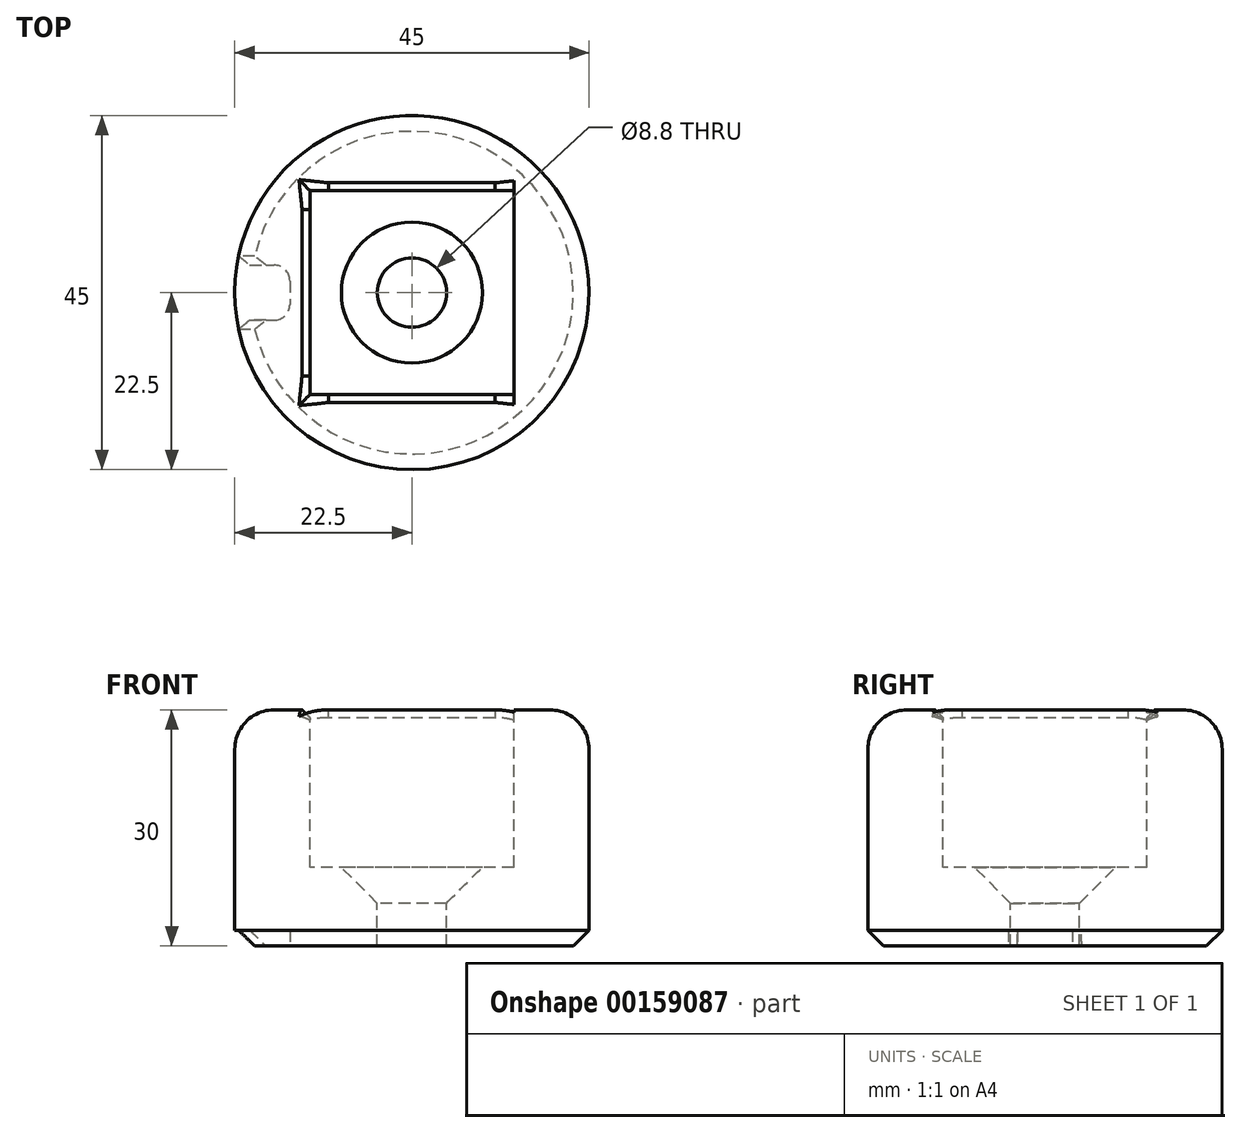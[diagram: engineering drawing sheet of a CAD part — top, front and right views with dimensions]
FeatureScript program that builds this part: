
annotation { "Feature Type Name" : "Feature", "Feature Type Description" : "" }
export const myFeature = defineFeature(function(context is Context, id is Id, definition is map)
    precondition{}
    {
        {
            var Q0;
            Q0=qCreatedBy(makeId("Top.planeOp"),FACE);
            var sketch = newSketch(context, id + "F0", { "sketchPlane" : qUnion([Q0])});
            skCircle(sketch, "E0", {"center": v(0, 0) * mm, "radius": 22.5 * mm});
            skSolve(sketch);
        }
        {
            var Q0;
            Q0=qSketchRegion(id+"F0",true);
            extrude(context, id + "F1", {"entities" : qUnion([Q0]), "depth" : 30 * mm});
        }
        {
            var Q0;
            Q0=makeQuery(id+"F1.opExtrude","CAP_FACE",FACE,{"disambiguationData":[OSD([sQuery(id+"F0.wireOp",EDGE,"E0")])],"isStart":false});
            var sketch = newSketch(context, id + "F2", { "sketchPlane" : qUnion([Q0])});
            skLineSegment(sketch, "E1.bottom", {"start": v(12.95, 12.95) * mm, "end": v(-12.95, 12.95) * mm});
            skLineSegment(sketch, "E1.top", {"start": v(12.95, -12.95) * mm, "end": v(-12.95, -12.95) * mm});
            skLineSegment(sketch, "E1.left", {"start": v(12.95, 12.95) * mm, "end": v(12.95, -12.95) * mm});
            skLineSegment(sketch, "E1.right", {"start": v(-12.95, 12.95) * mm, "end": v(-12.95, -12.95) * mm});
            skPoint(sketch, "E1.middle", {"position": v(0, 0) * mm});
            skSolve(sketch);
        }
        {
            var Q0;
            Q0=qSketchRegion(id+"F2",true);
            extrude(context, id + "F3", {"entities" : qUnion([Q0]), "operationType" : NewBodyOperationType.REMOVE, "oppositeDirection" : true, "depth" : 20 * mm});
        }
        {
            var Q0;
            Q0=makeQuery(id+"F1.opExtrude","CAP_EDGE",EDGE,{"disambiguationData":[OSD([sQuery(id+"F0.wireOp",EDGE,"E0")])],"isStart":true});
            chamfer(context, id + "F4", {"entities" : qUnion([Q0]), "width" : 2 * mm, "tangentPropagation" : true});
        }
        {
            var Q0;
            Q0=makeQuery(id+"F1.opExtrude","CAP_EDGE",EDGE,{"disambiguationData":[OSD([sQuery(id+"F0.wireOp",EDGE,"E0")])],"isStart":false});
            fillet(context, id + "F5", {"entities" : qUnion([Q0]), "radius" : 5 * mm, "tangentPropagation" : true, "allowEdgeOverflow" : false});
        }
        {
            var Q0;
            Q0=makeQuery(id+"F3.boolean.opBoolean","COPY",FACE,{"derivedFrom":makeQuery(id+"F3.opExtrude","CAP_FACE",FACE,{"disambiguationData":[OSD([sQuery(id+"F2.wireOp",EDGE,"E1.bottom"),sQuery(id+"F2.wireOp",EDGE,"E1.top"),sQuery(id+"F2.wireOp",EDGE,"E1.left"),sQuery(id+"F2.wireOp",EDGE,"E1.right")])],"isStart":false})});
            var sketch = newSketch(context, id + "F6", { "sketchPlane" : qUnion([Q0])});
            skPoint(sketch, "E2", {"position": v(0, 0) * mm});
            skSolve(sketch);
        }
        {
            var Q0;
            Q0=sQuery(id+"F6.wireOp",VERTEX,"E2");
            var Q1;
            Q1=makeQuery(id+"F1.opExtrude","SWEPT_BODY",BODY,{"disambiguationData":[OSD([sQuery(id+"F0.wireOp",EDGE,"E0")])]});
            hole(context, id + "F7", {"style" : HoleStyle.C_SINK, "endStyle" : HoleEndStyle.THROUGH, "standardTappedOrClearance" : lookupTablePath({ "standard" : "ISO", "fit" : "Normal", "size" : "M8", "type" : "Clearance" }), "standardBlindInLast" : lookupTablePath({ "fit" : "Standard", "standard" : "ISO", "size" : "M8", "type" : "Clearance" }), "holeDiameter" : 8.8 * mm, "cSinkDiameter" : 17.92 * mm, "cSinkAngle" : 90 * degree, "locations" : qUnion([Q0]), "scope" : qUnion([Q1]), "isTappedThrough" : true});
        }
        {
            var Q0;
            Q0=makeQuery(id+"F3.boolean.opBoolean","COPY",EDGE,{"derivedFrom":makeQuery(id+"F3.opExtrude","CAP_EDGE",EDGE,{"disambiguationData":[OSD([sQuery(id+"F2.wireOp",EDGE,"E1.right")])],"isStart":true})});
            var Q1;
            Q1=makeQuery(id+"F3.boolean.opBoolean","COPY",EDGE,{"derivedFrom":makeQuery(id+"F3.opExtrude","CAP_EDGE",EDGE,{"disambiguationData":[OSD([sQuery(id+"F2.wireOp",EDGE,"E1.bottom")])],"isStart":true})});
            var Q2;
            Q2=makeQuery(id+"F3.boolean.opBoolean","COPY",EDGE,{"derivedFrom":makeQuery(id+"F3.opExtrude","CAP_EDGE",EDGE,{"disambiguationData":[OSD([sQuery(id+"F2.wireOp",EDGE,"E1.left")])],"isStart":true})});
            var Q3;
            Q3=makeQuery(id+"F3.boolean.opBoolean","COPY",EDGE,{"derivedFrom":makeQuery(id+"F3.opExtrude","CAP_EDGE",EDGE,{"disambiguationData":[OSD([sQuery(id+"F2.wireOp",EDGE,"E1.top")])],"isStart":true})});
            var Q4;
            Q4=makeQuery(id+"F5.opFillet","BLEND_EDGE",EDGE,{"disambiguationData":[OD(1.0)],"blendedFrom":[makeQuery(id+"F1.opExtrude","CAP_EDGE",EDGE,{"disambiguationData":[OSD([sQuery(id+"F0.wireOp",EDGE,"E0")])],"isStart":false}),makeQuery(id+"F3.boolean.opBoolean","COPY",FACE,{"derivedFrom":makeQuery(id+"F3.opExtrude","SWEPT_FACE",FACE,{"disambiguationData":[OSD([sQuery(id+"F2.wireOp",EDGE,"E1.right")])]})})],"blendedInto":[makeQuery(id+"F3.boolean.opBoolean","COPY",FACE,{"derivedFrom":makeQuery(id+"F3.opExtrude","SWEPT_FACE",FACE,{"disambiguationData":[OSD([sQuery(id+"F2.wireOp",EDGE,"E1.right")])]})})]});
            var Q5;
            Q5=makeQuery(id+"F5.opFillet","BLEND_EDGE",EDGE,{"disambiguationData":[OD(1.0)],"blendedFrom":[makeQuery(id+"F1.opExtrude","CAP_EDGE",EDGE,{"disambiguationData":[OSD([sQuery(id+"F0.wireOp",EDGE,"E0")])],"isStart":false}),makeQuery(id+"F3.boolean.opBoolean","COPY",FACE,{"derivedFrom":makeQuery(id+"F3.opExtrude","SWEPT_FACE",FACE,{"disambiguationData":[OSD([sQuery(id+"F2.wireOp",EDGE,"E1.top")])]})})],"blendedInto":[makeQuery(id+"F3.boolean.opBoolean","COPY",FACE,{"derivedFrom":makeQuery(id+"F3.opExtrude","SWEPT_FACE",FACE,{"disambiguationData":[OSD([sQuery(id+"F2.wireOp",EDGE,"E1.top")])]})})]});
            var Q6;
            Q6=makeQuery(id+"F5.opFillet","BLEND_EDGE",EDGE,{"disambiguationData":[OD(0.0)],"blendedFrom":[makeQuery(id+"F1.opExtrude","CAP_EDGE",EDGE,{"disambiguationData":[OSD([sQuery(id+"F0.wireOp",EDGE,"E0")])],"isStart":false}),makeQuery(id+"F3.boolean.opBoolean","COPY",FACE,{"derivedFrom":makeQuery(id+"F3.opExtrude","SWEPT_FACE",FACE,{"disambiguationData":[OSD([sQuery(id+"F2.wireOp",EDGE,"E1.right")])]})})],"blendedInto":[makeQuery(id+"F3.boolean.opBoolean","COPY",FACE,{"derivedFrom":makeQuery(id+"F3.opExtrude","SWEPT_FACE",FACE,{"disambiguationData":[OSD([sQuery(id+"F2.wireOp",EDGE,"E1.right")])]})})]});
            var Q7;
            Q7=makeQuery(id+"F5.opFillet","BLEND_EDGE",EDGE,{"disambiguationData":[OD(1.0)],"blendedFrom":[makeQuery(id+"F1.opExtrude","CAP_EDGE",EDGE,{"disambiguationData":[OSD([sQuery(id+"F0.wireOp",EDGE,"E0")])],"isStart":false}),makeQuery(id+"F3.boolean.opBoolean","COPY",FACE,{"derivedFrom":makeQuery(id+"F3.opExtrude","SWEPT_FACE",FACE,{"disambiguationData":[OSD([sQuery(id+"F2.wireOp",EDGE,"E1.bottom")])]})})],"blendedInto":[makeQuery(id+"F3.boolean.opBoolean","COPY",FACE,{"derivedFrom":makeQuery(id+"F3.opExtrude","SWEPT_FACE",FACE,{"disambiguationData":[OSD([sQuery(id+"F2.wireOp",EDGE,"E1.bottom")])]})})]});
            chamfer(context, id + "F8", {"entities" : qUnion([Q0, Q1, Q2, Q3, Q4, Q5, Q6, Q7]), "width" : 1 * mm, "tangentPropagation" : true});
        }
        {
            var Q0;
            Q0=makeQuery(id+"F1.opExtrude","CAP_FACE",FACE,{"disambiguationData":[OSD([sQuery(id+"F0.wireOp",EDGE,"E0")])],"isStart":true});
            var sketch = newSketch(context, id + "F9", { "sketchPlane" : qUnion([Q0])});
            skLineSegment(sketch, "E3.bottom", {"start": v(-25.5, -3.5) * mm, "end": v(-17.5, -3.5) * mm});
            skLineSegment(sketch, "E3.top", {"start": v(-25.5, 3.5) * mm, "end": v(-17.5, 3.5) * mm});
            skLineSegment(sketch, "E3.left", {"start": v(-25.5, -3.5) * mm, "end": v(-25.5, 3.5) * mm});
            skLineSegment(sketch, "E3.right", {"start": v(-15.5, -1.5) * mm, "end": v(-15.5, 1.5) * mm});
            skPoint(sketch, "E3.middle", {"position": v(-20.5, 0) * mm});
            skPoint(sketch, "E4.visualSharp", {"position": v(-15.5, -3.5) * mm});
            skArc(sketch, "E4.filletArc", {"start": v(-17.5, -3.5) * mm, "mid": v(-16.09, -2.91) * mm, "end": v(-15.5, -1.5) * mm});
            skPoint(sketch, "E5.visualSharp", {"position": v(-15.5, 3.5) * mm});
            skArc(sketch, "E5.filletArc", {"start": v(-15.5, 1.5) * mm, "mid": v(-16.09, 2.91) * mm, "end": v(-17.5, 3.5) * mm});
            skSolve(sketch);
        }
        {
            var Q0;
            Q0 = qSketchRegion(id + "F9", true);
            extrude(context, id + "F10", {"entities" : qUnion([Q0]), "operationType" : NewBodyOperationType.REMOVE, "oppositeDirection" : true, "depth" : 2 * mm});
        }
        {
            var Q0;
            Q0=makeQuery(id+"F10.boolean.opBoolean","INTERSECT",EDGE,{"derivedFrom":[makeQuery(id+"F4.opChamfer","BLEND_FACE",FACE,{"disambiguationData":[OSD([sQuery(id+"F0.wireOp",EDGE,"E0")])]}),makeQuery(id+"F10.opExtrude","SWEPT_FACE",FACE,{"disambiguationData":[OSD([sQuery(id+"F9.wireOp",EDGE,"E3.bottom")])]})]});
            var Q1;
            Q1=makeQuery(id+"F10.boolean.opBoolean","COPY",EDGE,{"derivedFrom":makeQuery(id+"F10.opExtrude","CAP_EDGE",EDGE,{"disambiguationData":[OSD([sQuery(id+"F9.wireOp",EDGE,"E3.bottom")])],"isStart":true})});
            var Q2;
            Q2=makeQuery(id+"F10.boolean.opBoolean","COPY",EDGE,{"derivedFrom":makeQuery(id+"F10.opExtrude","CAP_EDGE",EDGE,{"disambiguationData":[OSD([sQuery(id+"F9.wireOp",EDGE,"E4.filletArc")])],"isStart":true})});
            var Q3;
            Q3=makeQuery(id+"F10.boolean.opBoolean","COPY",EDGE,{"derivedFrom":makeQuery(id+"F10.opExtrude","CAP_EDGE",EDGE,{"disambiguationData":[OSD([sQuery(id+"F9.wireOp",EDGE,"E3.right")])],"isStart":true})});
            var Q4;
            Q4=makeQuery(id+"F10.boolean.opBoolean","COPY",EDGE,{"derivedFrom":makeQuery(id+"F10.opExtrude","CAP_EDGE",EDGE,{"disambiguationData":[OSD([sQuery(id+"F9.wireOp",EDGE,"E5.filletArc")])],"isStart":true})});
            var Q5;
            Q5=makeQuery(id+"F10.boolean.opBoolean","COPY",EDGE,{"derivedFrom":makeQuery(id+"F10.opExtrude","CAP_EDGE",EDGE,{"disambiguationData":[OSD([sQuery(id+"F9.wireOp",EDGE,"E3.top")])],"isStart":true})});
            var Q6;
            Q6=makeQuery(id+"F10.boolean.opBoolean","INTERSECT",EDGE,{"derivedFrom":[makeQuery(id+"F4.opChamfer","BLEND_FACE",FACE,{"disambiguationData":[OSD([sQuery(id+"F0.wireOp",EDGE,"E0")])]}),makeQuery(id+"F10.opExtrude","SWEPT_FACE",FACE,{"disambiguationData":[OSD([sQuery(id+"F9.wireOp",EDGE,"E3.top")])]})]});
            chamfer(context, id + "F11", {"entities" : qUnion([Q0, Q1, Q2, Q3, Q4, Q5, Q6]), "width" : 1 * mm, "tangentPropagation" : true});
        }
    });
